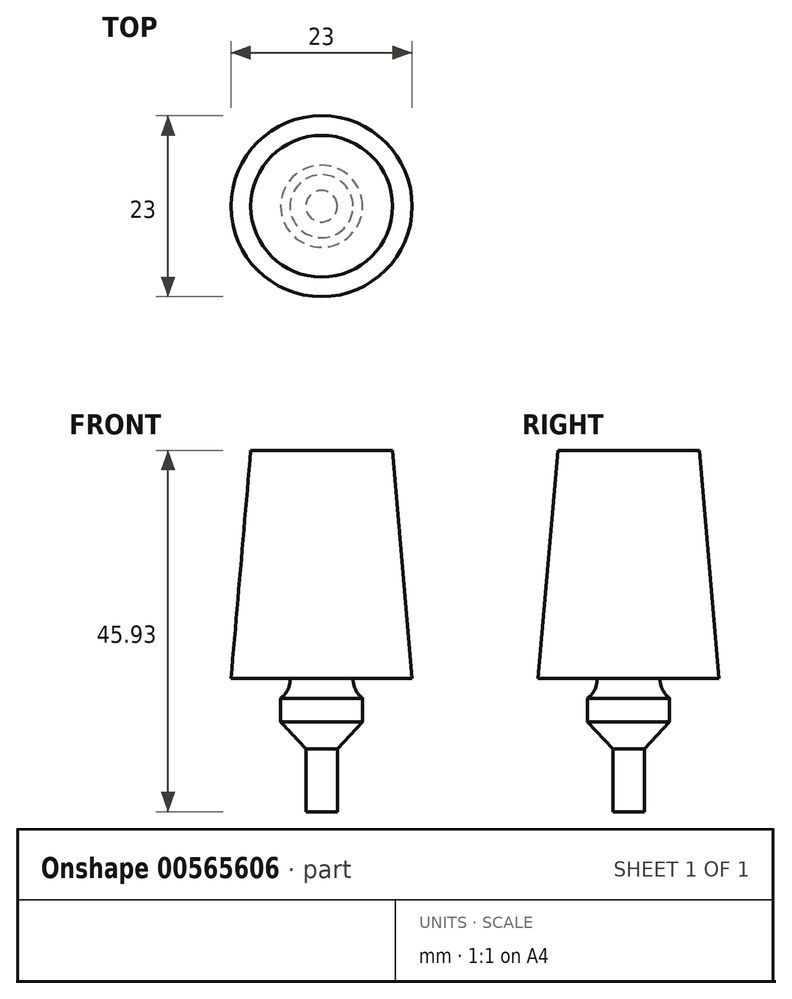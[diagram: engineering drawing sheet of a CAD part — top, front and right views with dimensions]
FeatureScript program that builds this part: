
annotation { "Feature Type Name" : "Feature", "Feature Type Description" : "" }
export const myFeature = defineFeature(function(context is Context, id is Id, definition is map)
    precondition{}
    {
        {
            var Q0;
            Q0=qCreatedBy(makeId("Front.planeOp"),FACE);
            var sketch = newSketch(context, id + "F0", { "sketchPlane" : qUnion([Q0])});
            skLineSegment(sketch, "E0", {"start": v(0, 0) * mm, "end": v(0, 29) * mm});
            skLineSegment(sketch, "E1", {"start": v(0, 29) * mm, "end": v(-9, 29) * mm});
            skLineSegment(sketch, "E2", {"start": v(-9, 29) * mm, "end": v(-11.5, 0) * mm});
            skLineSegment(sketch, "E3", {"start": v(-11.5, 0) * mm, "end": v(-4, 0) * mm});
            skLineSegment(sketch, "E4", {"start": v(-4, 0) * mm, "end": v(-4, -2.5) * mm});
            skLineSegment(sketch, "E5", {"start": v(-4, -2.5) * mm, "end": v(-5.2, -2.5) * mm});
            skLineSegment(sketch, "E6", {"start": v(-5.2, -2.5) * mm, "end": v(-5.2, -5.5) * mm});
            skLineSegment(sketch, "E7", {"start": v(-5.2, -5.5) * mm, "end": v(-2, -8.93) * mm});
            skLineSegment(sketch, "E8", {"start": v(-2, -8.93) * mm, "end": v(-2, -16.93) * mm});
            skLineSegment(sketch, "E9", {"start": v(-2, -16.93) * mm, "end": v(0, -16.93) * mm});
            skLineSegment(sketch, "E10", {"start": v(0, -16.93) * mm, "end": v(0, 0) * mm});
            skSolve(sketch);
        }
        {
            var Q0;
            Q0 = qSketchRegion(id + "F0", true);
            var Q1;
            Q1=sQuery(id+"F0.wireOp",EDGE,"E0");
            revolve(context, id + "F1", {"entities" : qUnion([Q0]), "axis" : qUnion([Q1]), "revolveType" : RevolveType.FULL});
        }
        {
            var Q0;
            Q0=makeQuery(id+"F1.opRevolve","SWEPT_EDGE",EDGE,{"disambiguationData":[OSD([sQuery(id+"F0.wireOp",EDGE,"E4"),sQuery(id+"F0.wireOp",EDGE,"E5")])]});
            fillet(context, id + "F2", {"entities" : qUnion([Q0]), "radius" : 3 * mm, "tangentPropagation" : true, "allowEdgeOverflow" : false});
        }
    });
